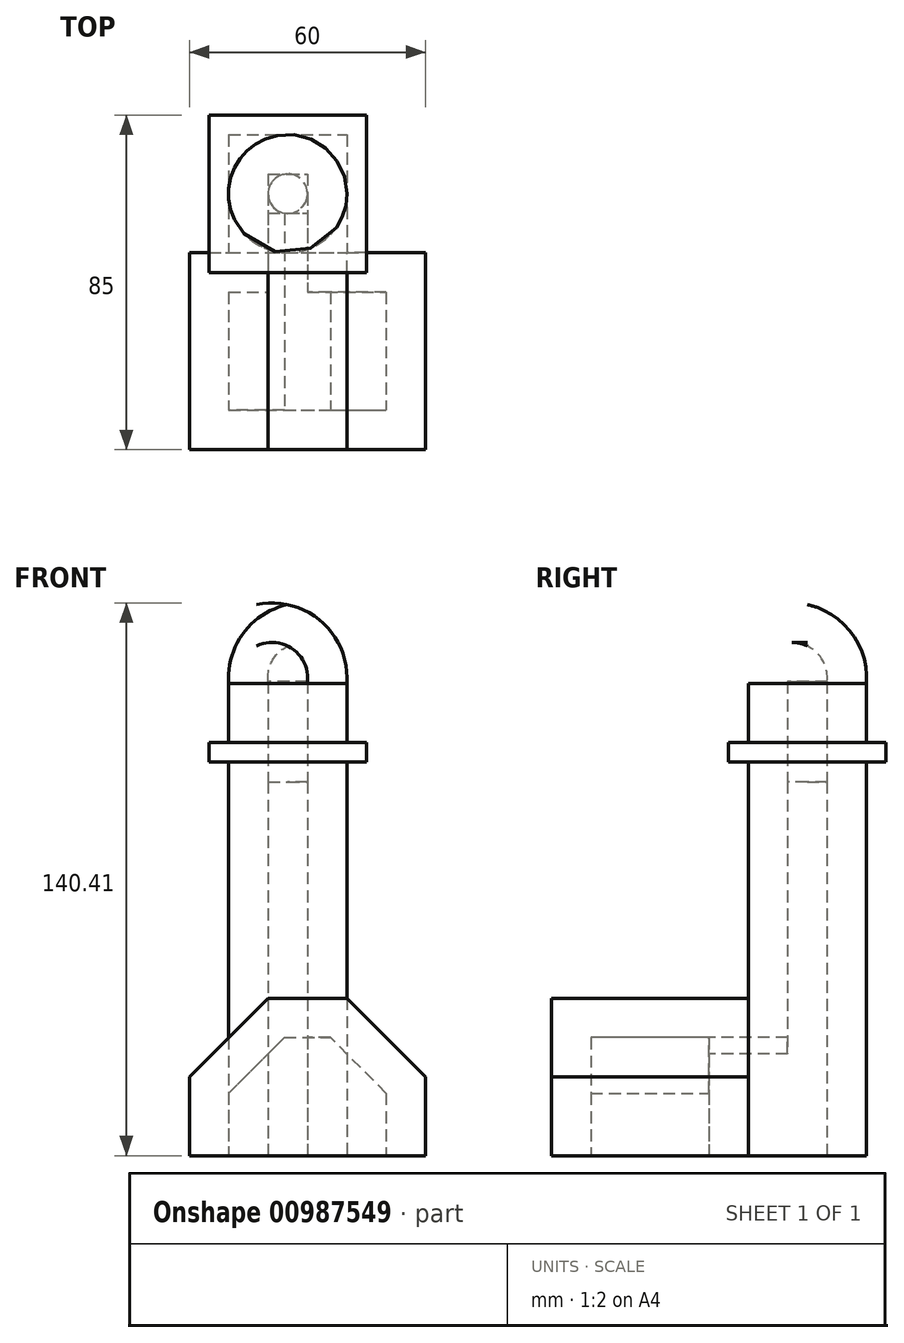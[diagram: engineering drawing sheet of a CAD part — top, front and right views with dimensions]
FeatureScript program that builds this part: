
annotation { "Feature Type Name" : "Feature", "Feature Type Description" : "" }
export const myFeature = defineFeature(function(context is Context, id is Id, definition is map)
    precondition{}
    {
        {
            var Q0;
            Q0=qCreatedBy(makeId("Top.planeOp"),FACE);
            var sketch = newSketch(context, id + "F0", { "sketchPlane" : qUnion([Q0])});
            skLineSegment(sketch, "E0.bottom", {"start": v(-15, 15) * mm, "end": v(15, 15) * mm});
            skLineSegment(sketch, "E0.top", {"start": v(-15, -15) * mm, "end": v(15, -15) * mm});
            skLineSegment(sketch, "E0.left", {"start": v(-15, 15) * mm, "end": v(-15, -15) * mm});
            skLineSegment(sketch, "E0.right", {"start": v(15, 15) * mm, "end": v(15, -15) * mm});
            skSolve(sketch);
        }
        {
            var Q0;
            Q0 = qSketchRegion(id + "F0", true);
            extrude(context, id + "F1", {"entities" : qUnion([Q0]), "depth" : 100 * mm, "offsetDistance" : 25 * mm});
        }
        {
            var Q0;
            Q0=makeQuery(id+"F1.opExtrude","CAP_FACE",FACE,{"disambiguationData":[OSD([sQuery(id+"F0.wireOp",EDGE,"E0.bottom"),sQuery(id+"F0.wireOp",EDGE,"E0.top"),sQuery(id+"F0.wireOp",EDGE,"E0.left"),sQuery(id+"F0.wireOp",EDGE,"E0.right"),sQuery(id+"F0.wireOp",EDGE,"2bf325f2-dc9f-4aea-bd7f-c49173ceb0f4.0"),sQuery(id+"F0.wireOp",EDGE,"2bf325f2-dc9f-4aea-bd7f-c49173ceb0f4.1"),sQuery(id+"F0.wireOp",EDGE,"2bf325f2-dc9f-4aea-bd7f-c49173ceb0f4.2"),sQuery(id+"F0.wireOp",EDGE,"2bf325f2-dc9f-4aea-bd7f-c49173ceb0f4.3")])],"isStart":false});
            var sketch = newSketch(context, id + "F2", { "sketchPlane" : qUnion([Q0])});
            skLineSegment(sketch, "E1.bottom", {"start": v(-20, 20) * mm, "end": v(20, 20) * mm});
            skLineSegment(sketch, "E1.top", {"start": v(-20, -20) * mm, "end": v(20, -20) * mm});
            skLineSegment(sketch, "E1.left", {"start": v(-20, 20) * mm, "end": v(-20, -20) * mm});
            skLineSegment(sketch, "E1.right", {"start": v(20, 20) * mm, "end": v(20, -20) * mm});
            skSolve(sketch);
        }
        {
            var Q0;
            Q0 = qSketchRegion(id + "F2", true);
            extrude(context, id + "F3", {"entities" : qUnion([Q0]), "operationType" : NewBodyOperationType.ADD, "depth" : (5) * mm, "offsetDistance" : 25 * mm});
        }
        {
            var Q0;
            Q0=makeQuery(id+"F3.opExtrude","CAP_FACE",FACE,{"disambiguationData":[OSD([sQuery(id+"F2.wireOp",EDGE,"E1.bottom"),sQuery(id+"F2.wireOp",EDGE,"E1.top"),sQuery(id+"F2.wireOp",EDGE,"E1.left"),sQuery(id+"F2.wireOp",EDGE,"E1.right")])],"isStart":false});
            var sketch = newSketch(context, id + "F4", { "sketchPlane" : qUnion([Q0])});
            skCircle(sketch, "E2", {"center": v(0, 0) * mm, "radius": 15 * mm});
            skSolve(sketch);
        }
        {
            var Q0;
            Q0=qCreatedBy(makeId("Front.planeOp"),FACE);
            var sketch = newSketch(context, id + "F5", { "sketchPlane" : qUnion([Q0])});
            skLineSegment(sketch, "E3", {"start": v(0, 105) * mm, "end": v(0, 140) * mm});
            skLineSegment(sketch, "E4", {"start": v(0, 105) * mm, "end": v(15, 105) * mm});
            skLineSegment(sketch, "E5", {"start": v(15, 105) * mm, "end": v(15, 120) * mm});
            skArc(sketch, "E6", {"start": v(15, 120) * mm, "mid": v(11.25, 132.81) * mm, "end": v(0, 140) * mm});
            skSolve(sketch);
        }
        {
            var Q0;
            Q0=makeQuery(id+"F5.imprint","IMPRINT",FACE,{"disambiguationData":[TD([[makeQuery(id+"F5.imprint","IMPRINT",EDGE,{"derivedFrom":sQuery(id+"F5.wireOp",EDGE,"E3")}),-1.0]])]});
            var Q1;
            Q1=sQuery(id+"F4.wireOp",EDGE,"E2");
            revolve(context, id + "F6", {"operationType" : NewBodyOperationType.ADD, "surfaceOperationType" : NewSurfaceOperationType.NEW, "entities" : qUnion([Q0]), "axis" : qUnion([Q1]), "revolveType" : RevolveType.FULL});
        }
        {
            var Q0;
            Q0=qCreatedBy(makeId("Top.planeOp"),FACE);
            var sketch = newSketch(context, id + "F7", { "sketchPlane" : qUnion([Q0])});
            skLineSegment(sketch, "E7.bottom", {"start": v(-25, -15) * mm, "end": v(35, -15) * mm});
            skLineSegment(sketch, "E7.top", {"start": v(-25, -65) * mm, "end": v(35, -65) * mm});
            skLineSegment(sketch, "E7.left", {"start": v(-25, -15) * mm, "end": v(-25, -65) * mm});
            skLineSegment(sketch, "E7.right", {"start": v(35, -15) * mm, "end": v(35, -65) * mm});
            skSolve(sketch);
        }
        {
            var Q0;
            Q0 = qSketchRegion(id + "F7", true);
            extrude(context, id + "F8", {"entities" : qUnion([Q0]), "operationType" : NewBodyOperationType.ADD, "depth" : 40 * mm, "offsetDistance" : 25 * mm});
        }
        {
            var Q0;
            Q0=makeQuery(id+"F8.opExtrude","CAP_EDGE",EDGE,{"disambiguationData":[OSD([sQuery(id+"F7.wireOp",EDGE,"E7.left")])],"isStart":false});
            var Q1;
            Q1=makeQuery(id+"F8.opExtrude","CAP_EDGE",EDGE,{"disambiguationData":[OSD([sQuery(id+"F7.wireOp",EDGE,"E7.right")])],"isStart":false});
            chamfer(context, id + "F9", {"entities" : qUnion([Q0, Q1]), "width" : 20 * mm, "tangentPropagation" : true});
        }
        {
            var Q0;
            Q0=makeQuery(id+"F8.boolean.opBoolean","MERGE",FACE,{"derivedFrom":[makeQuery(id+"F1.opExtrude","CAP_FACE",FACE,{"disambiguationData":[OSD([sQuery(id+"F0.wireOp",EDGE,"E0.bottom"),sQuery(id+"F0.wireOp",EDGE,"E0.top"),sQuery(id+"F0.wireOp",EDGE,"E0.left"),sQuery(id+"F0.wireOp",EDGE,"E0.right"),sQuery(id+"F0.wireOp",EDGE,"2bf325f2-dc9f-4aea-bd7f-c49173ceb0f4.0"),sQuery(id+"F0.wireOp",EDGE,"2bf325f2-dc9f-4aea-bd7f-c49173ceb0f4.1"),sQuery(id+"F0.wireOp",EDGE,"2bf325f2-dc9f-4aea-bd7f-c49173ceb0f4.2"),sQuery(id+"F0.wireOp",EDGE,"2bf325f2-dc9f-4aea-bd7f-c49173ceb0f4.3")])],"isStart":true}),makeQuery(id+"F8.opExtrude","CAP_FACE",FACE,{"disambiguationData":[OSD([sQuery(id+"F7.wireOp",EDGE,"E7.bottom"),sQuery(id+"F7.wireOp",EDGE,"E7.top"),sQuery(id+"F7.wireOp",EDGE,"E7.left"),sQuery(id+"F7.wireOp",EDGE,"E7.right")])],"isStart":true})]});
            shell(context, id + "F10", {"entities" : qUnion([Q0]), "thickness" : 10 * mm});
        }
    });
